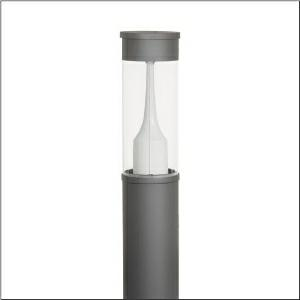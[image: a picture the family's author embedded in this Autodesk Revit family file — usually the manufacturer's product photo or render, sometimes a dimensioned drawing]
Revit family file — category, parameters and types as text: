
# Revit family: city-light_400_iq___p1_0a_5xa5305bf14h_2d73
name_source: partatom
category: Lighting Fixtures
units: mm (PartAtom-declared; Revit-internal decimal feet)

## family parameters
Cut with Voids When Loaded = No
Host = Face
Light Source = No
Part Type = Normal
Room Calculation Point = No
Round Connector Dimension = Use Diameter
Shared = No

## types (1)
- --- (1 x LED, 1510 lm, 12.9 W, 2200K)
    Apparent Load = 13 VA
    CIE Flux Codes = 32 61 90 93 100
    Color Rendering = 70
    Color Temperature = 2200K
    Default Elevation = 1800 mm
    Description = City-Light 400 iQ, light pillar, Module 540 iQ-SR, primary light control with 3 zone facetted reflector, of plastic, silver coated, highly specular, structured, primary optical cover: cover, of PMMA, transparent, partly coated, light distribution: P1.0a, primary light characteristic: strongly asymmetric, LED, High Power LED, rated luminous flux: 1.510lm, luminous efficacy: 117lm/W, light colour: 722, colour temperature: 2200K, control gear: ECG iQ, control: presetting dimming logarithmic, Street-Remote, Auto-Match, Temp-Guard, Lumen-Switch, Night-Set, Smart-Wire, Light-Fading, Desk-Remote (wireless, voltage-free reading and setting of iQ features in the workshop via application-optimized NFC function/RFID function), optimised constant luminous flux control (CLO 2.0), with terminal, 6-pole, max. 2.5mm², mains connection: 220..240V, AC, 50/60Hz, start of lifetime: 13W, end of lifetime: 13W, reduction: 6W, luminaire housing, cylindrical, of extruded aluminium section, coated, Siteco® metallic grey (DB 702S), length: 4.694mm, diameter: 200mm, Module 540 iQ-SR, traffic white (RAL 9016), equipment: standard, protection rating (complete): IP65, insulation class (complete): insulation class II (safety insulation), certification: CE, ENEC, VDE, packaging unit: 1 piece

Light Distribution: P1.0a
    Height = 500 mm
    Lamp = 1 x LED
    Lamp Light Flux = 1510 lm
    Lamp Power = 12.9 W
    Lamp count = 1
    Length = 200 mm
    Luminous efficacy = 117 lm/W
    Manufacturer = Siteco
    ModVariant = No
    Model = 5XA5305BF14H
    Mounting Place = Floor
    Mounting Type = Freestanding
    Number of Poles = 1
    OnlyDefault = Yes
    Power Factor = 1
    Product Name = City-Light 400 iQ | P1.0a
    Product group = light pillar | freestanding
    ProductGroupID = 1301
    Protection Class = Protection class II
    Protection Degree = IP 65
    RLX_Detail_Level = 1
    RlxData = <blob elided: 75385 chars, md5=f312a435>
    Socket = socket
    Standby Power = 0 W
    System Light Flux = 1510 lm
    System Power = 13 W
    Type Comments = factory setting: luminous flux: 100 % | dim-lin: 254 | 516 mA
    Type Image = l_1006914.jpg
    URL = http://relux.com
    VarID = @adj_070677
    Voltage = 0 V
    Weight = 0.00 kg
    Width = 0 mm  [stored 0 ft]

note: [stored X ft] marks values corroborated as IEEE doubles in the binary element streams (Revit-internal decimal feet)

## geometry (parser evidence)
native form markers: Blend x4, Sweep x10
no freeform markers — native parametric forms only
